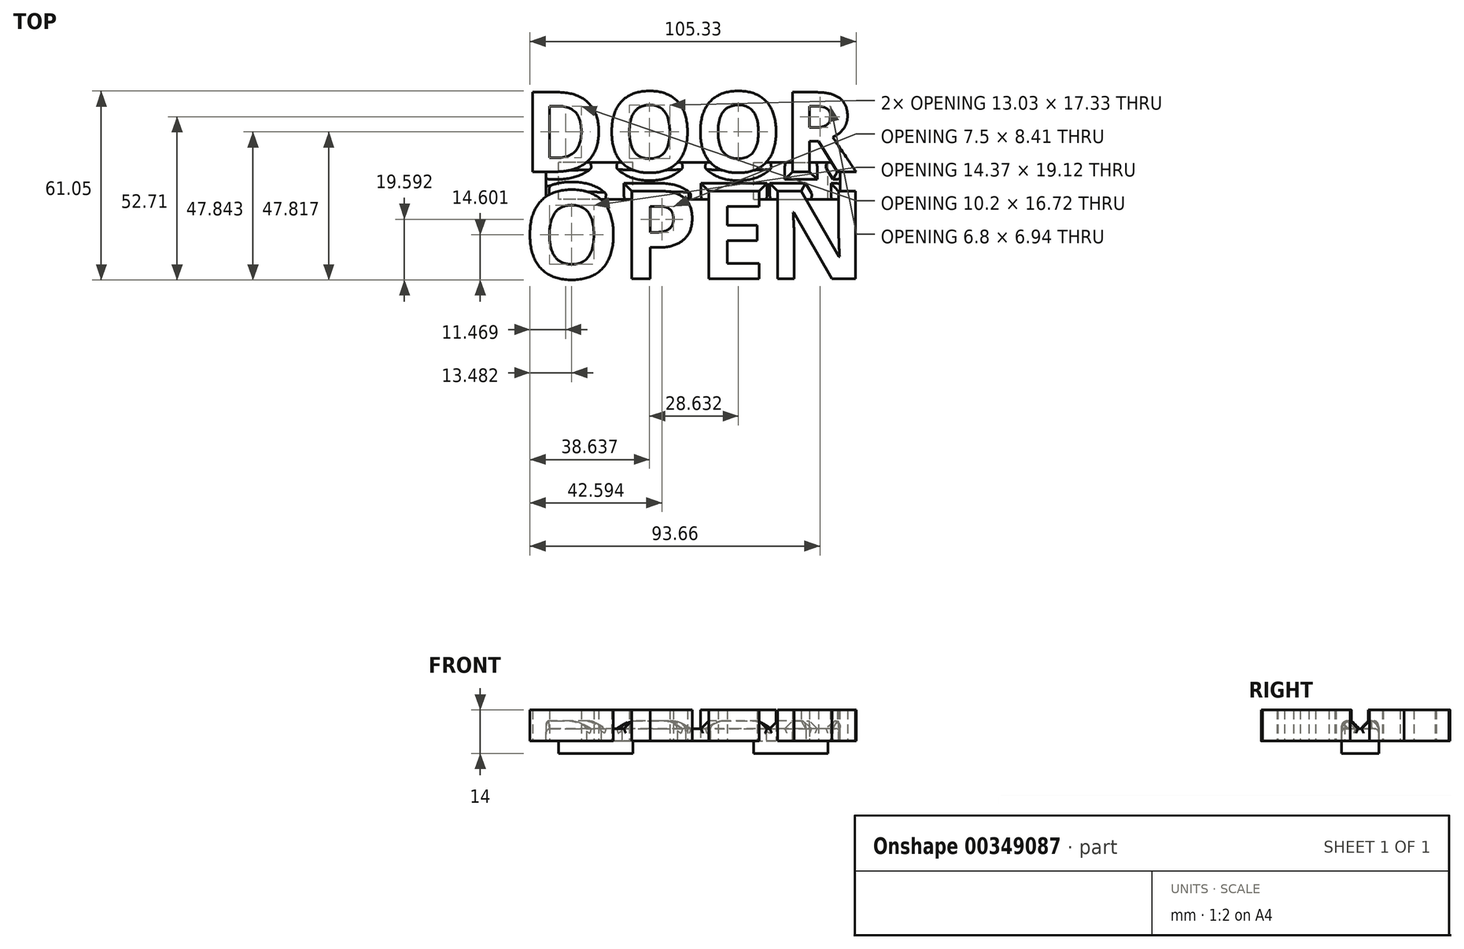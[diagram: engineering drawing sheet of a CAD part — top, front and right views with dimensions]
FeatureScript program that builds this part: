
annotation { "Feature Type Name" : "Feature", "Feature Type Description" : "" }
export const myFeature = defineFeature(function(context is Context, id is Id, definition is map)
    precondition{}
    {
        {
            var Q0;
            Q0=qCreatedBy(makeId("Top.planeOp"),FACE);
            var sketch = newSketch(context, id + "F0", { "sketchPlane" : qUnion([Q0])});
            skText(sketch, "E0", { "text": "DOOR", "fontName": "OpenSans-Bold.ttf"});
            skText(sketch, "E1", { "text": "OPEN", "fontName": "OpenSans-Bold.ttf"});
            skLineSegment(sketch, "E2", {"start": v(0, 3) * mm, "end": v(0, -3) * mm, "construction": true});
            skPoint(sketch, "E3", {"position": v(0, 0) * mm});
            const initialGuessF0  = {"E0": [-0.055, 0.003, 1, 0, 0.0259], "E1": [-0.055, -0.03157, 1, 0, 0.02857]};
            skSetInitialGuess(sketch, initialGuessF0);
            skSolve(sketch);
        }
        {
            var Q0;
            Q0=makeQuery(id+"F0.imprint","IMPRINT",FACE,{"disambiguationData":[TD([[makeQuery(id+"F0.imprint","IMPRINT",EDGE,{"derivedFrom":sQuery(id+"F0.wireOp",EDGE,"E0.sketch_text.stroke-0")}),-1.0]])]});
            var Q1;
            Q1=makeQuery(id+"F0.imprint","IMPRINT",FACE,{"disambiguationData":[TD([[makeQuery(id+"F0.imprint","IMPRINT",EDGE,{"derivedFrom":sQuery(id+"F0.wireOp",EDGE,"E0.sketch_text.stroke-12")}),-1.0]])]});
            var Q2;
            Q2=makeQuery(id+"F0.imprint","IMPRINT",FACE,{"disambiguationData":[TD([[makeQuery(id+"F0.imprint","IMPRINT",EDGE,{"derivedFrom":sQuery(id+"F0.wireOp",EDGE,"E0.sketch_text.stroke-26")}),-1.0]])]});
            var Q3;
            Q3=makeQuery(id+"F0.imprint","IMPRINT",FACE,{"disambiguationData":[TD([[makeQuery(id+"F0.imprint","IMPRINT",EDGE,{"derivedFrom":sQuery(id+"F0.wireOp",EDGE,"E0.sketch_text.stroke-40")}),-1.0]])]});
            var Q4;
            Q4=makeQuery(id+"F0.imprint","IMPRINT",FACE,{"disambiguationData":[TD([[makeQuery(id+"F0.imprint","IMPRINT",EDGE,{"derivedFrom":sQuery(id+"F0.wireOp",EDGE,"E1.sketch_text.stroke-0")}),-1.0]])]});
            var Q5;
            Q5=makeQuery(id+"F0.imprint","IMPRINT",FACE,{"disambiguationData":[TD([[makeQuery(id+"F0.imprint","IMPRINT",EDGE,{"derivedFrom":sQuery(id+"F0.wireOp",EDGE,"E1.sketch_text.stroke-14")}),-1.0]])]});
            var Q6;
            Q6=makeQuery(id+"F0.imprint","IMPRINT",FACE,{"disambiguationData":[TD([[makeQuery(id+"F0.imprint","IMPRINT",EDGE,{"derivedFrom":sQuery(id+"F0.wireOp",EDGE,"E1.sketch_text.stroke-30")}),-1.0]])]});
            var Q7;
            Q7=makeQuery(id+"F0.imprint","IMPRINT",FACE,{"disambiguationData":[TD([[makeQuery(id+"F0.imprint","IMPRINT",EDGE,{"derivedFrom":sQuery(id+"F0.wireOp",EDGE,"E1.sketch_text.stroke-42")}),-1.0]])]});
            extrude(context, id + "F1", {"entities" : qUnion([Q0, Q1, Q2, Q3, Q4, Q5, Q6, Q7]), "depth" : 10 * mm});
        }
        {
            var Q0;
            Q0=qCreatedBy(makeId("Top.planeOp"),FACE);
            var sketch = newSketch(context, id + "F2", { "sketchPlane" : qUnion([Q0])});
            skLineSegment(sketch, "E4.bottom", {"start": v(47.5, 6) * mm, "end": v(-47.5, 6) * mm});
            skLineSegment(sketch, "E4.top", {"start": v(47.5, -6) * mm, "end": v(-47.5, -6) * mm});
            skLineSegment(sketch, "E4.left", {"start": v(47.5, 6) * mm, "end": v(47.5, -6) * mm});
            skLineSegment(sketch, "E4.right", {"start": v(-47.5, 6) * mm, "end": v(-47.5, -6) * mm});
            skPoint(sketch, "E4.middle", {"position": v(0, 0) * mm});
            skSolve(sketch);
        }
        {
            var Q0;
            Q0=makeQuery(id+"F2.imprint","IMPRINT",FACE,{"disambiguationData":[TD([[makeQuery(id+"F2.imprint","IMPRINT",EDGE,{"derivedFrom":sQuery(id+"F2.wireOp",EDGE,"E4.bottom")}),1.0]])]});
            extrude(context, id + "F3", {"entities" : qUnion([Q0]), "operationType" : NewBodyOperationType.ADD, "depth" : 4 * mm});
        }
        {
            var Q0;
            Q0=makeQuery(id+"F3.boolean.opBoolean","INTERSECT",EDGE,{"derivedFrom":[makeQuery(id+"F1.opExtrude","SWEPT_FACE",FACE,{"disambiguationData":[OSD([sQuery(id+"F0.wireOp",EDGE,"E0.sketch_text.stroke-1")])]}),makeQuery(id+"F3.opExtrude","CAP_FACE",FACE,{"disambiguationData":[OSD([sQuery(id+"F2.wireOp",EDGE,"E4.bottom"),sQuery(id+"F2.wireOp",EDGE,"E4.top"),sQuery(id+"F2.wireOp",EDGE,"E4.left"),sQuery(id+"F2.wireOp",EDGE,"E4.right")])],"isStart":false})]});
            var Q1;
            Q1=makeQuery(id+"F3.boolean.opBoolean","INTERSECT",EDGE,{"derivedFrom":[makeQuery(id+"F1.opExtrude","SWEPT_FACE",FACE,{"disambiguationData":[OSD([sQuery(id+"F0.wireOp",EDGE,"E0.sketch_text.stroke-14")])]}),makeQuery(id+"F3.opExtrude","CAP_FACE",FACE,{"disambiguationData":[OSD([sQuery(id+"F2.wireOp",EDGE,"E4.bottom"),sQuery(id+"F2.wireOp",EDGE,"E4.top"),sQuery(id+"F2.wireOp",EDGE,"E4.left"),sQuery(id+"F2.wireOp",EDGE,"E4.right")])],"isStart":false})]});
            var Q2;
            Q2=makeQuery(id+"F3.boolean.opBoolean","INTERSECT",EDGE,{"derivedFrom":[makeQuery(id+"F1.opExtrude","SWEPT_FACE",FACE,{"disambiguationData":[OSD([sQuery(id+"F0.wireOp",EDGE,"E0.sketch_text.stroke-28")])]}),makeQuery(id+"F3.opExtrude","CAP_FACE",FACE,{"disambiguationData":[OSD([sQuery(id+"F2.wireOp",EDGE,"E4.bottom"),sQuery(id+"F2.wireOp",EDGE,"E4.top"),sQuery(id+"F2.wireOp",EDGE,"E4.left"),sQuery(id+"F2.wireOp",EDGE,"E4.right")])],"isStart":false})]});
            var Q3;
            Q3=makeQuery(id+"F3.boolean.opBoolean","INTERSECT",EDGE,{"derivedFrom":[makeQuery(id+"F1.opExtrude","SWEPT_FACE",FACE,{"disambiguationData":[OSD([sQuery(id+"F0.wireOp",EDGE,"E0.sketch_text.stroke-48")])]}),makeQuery(id+"F3.opExtrude","CAP_FACE",FACE,{"disambiguationData":[OSD([sQuery(id+"F2.wireOp",EDGE,"E4.bottom"),sQuery(id+"F2.wireOp",EDGE,"E4.top"),sQuery(id+"F2.wireOp",EDGE,"E4.left"),sQuery(id+"F2.wireOp",EDGE,"E4.right")])],"isStart":false})]});
            var Q4;
            Q4=makeQuery(id+"F3.boolean.opBoolean","INTERSECT",EDGE,{"derivedFrom":[makeQuery(id+"F1.opExtrude","SWEPT_FACE",FACE,{"disambiguationData":[OSD([sQuery(id+"F0.wireOp",EDGE,"E0.sketch_text.stroke-49")])]}),makeQuery(id+"F3.opExtrude","CAP_FACE",FACE,{"disambiguationData":[OSD([sQuery(id+"F2.wireOp",EDGE,"E4.bottom"),sQuery(id+"F2.wireOp",EDGE,"E4.top"),sQuery(id+"F2.wireOp",EDGE,"E4.left"),sQuery(id+"F2.wireOp",EDGE,"E4.right")])],"isStart":false})]});
            var Q5;
            Q5=makeQuery(id+"F3.boolean.opBoolean","INTERSECT",EDGE,{"derivedFrom":[makeQuery(id+"F1.opExtrude","SWEPT_FACE",FACE,{"disambiguationData":[OSD([sQuery(id+"F0.wireOp",EDGE,"E0.sketch_text.stroke-47")])]}),makeQuery(id+"F3.opExtrude","CAP_FACE",FACE,{"disambiguationData":[OSD([sQuery(id+"F2.wireOp",EDGE,"E4.bottom"),sQuery(id+"F2.wireOp",EDGE,"E4.top"),sQuery(id+"F2.wireOp",EDGE,"E4.left"),sQuery(id+"F2.wireOp",EDGE,"E4.right")])],"isStart":false})]});
            var Q6;
            Q6=makeQuery(id+"F3.boolean.opBoolean","INTERSECT",EDGE,{"derivedFrom":[makeQuery(id+"F1.opExtrude","SWEPT_FACE",FACE,{"disambiguationData":[OSD([sQuery(id+"F0.wireOp",EDGE,"E0.sketch_text.stroke-57")])]}),makeQuery(id+"F3.opExtrude","CAP_FACE",FACE,{"disambiguationData":[OSD([sQuery(id+"F2.wireOp",EDGE,"E4.bottom"),sQuery(id+"F2.wireOp",EDGE,"E4.top"),sQuery(id+"F2.wireOp",EDGE,"E4.left"),sQuery(id+"F2.wireOp",EDGE,"E4.right")])],"isStart":false})]});
            var Q7;
            Q7=makeQuery(id+"F3.boolean.opBoolean","INTERSECT",EDGE,{"derivedFrom":[makeQuery(id+"F1.opExtrude","SWEPT_FACE",FACE,{"disambiguationData":[OSD([sQuery(id+"F0.wireOp",EDGE,"E0.sketch_text.stroke-56")])]}),makeQuery(id+"F3.opExtrude","CAP_FACE",FACE,{"disambiguationData":[OSD([sQuery(id+"F2.wireOp",EDGE,"E4.bottom"),sQuery(id+"F2.wireOp",EDGE,"E4.top"),sQuery(id+"F2.wireOp",EDGE,"E4.left"),sQuery(id+"F2.wireOp",EDGE,"E4.right")])],"isStart":false})]});
            var Q8;
            Q8=makeQuery(id+"F3.boolean.opBoolean","INTERSECT",EDGE,{"derivedFrom":[makeQuery(id+"F1.opExtrude","SWEPT_FACE",FACE,{"disambiguationData":[OSD([sQuery(id+"F0.wireOp",EDGE,"E1.sketch_text.stroke-53")])]}),makeQuery(id+"F3.opExtrude","CAP_FACE",FACE,{"disambiguationData":[OSD([sQuery(id+"F2.wireOp",EDGE,"E4.bottom"),sQuery(id+"F2.wireOp",EDGE,"E4.top"),sQuery(id+"F2.wireOp",EDGE,"E4.left"),sQuery(id+"F2.wireOp",EDGE,"E4.right")])],"isStart":false})]});
            var Q9;
            Q9=makeQuery(id+"F3.boolean.opBoolean","INTERSECT",EDGE,{"derivedFrom":[makeQuery(id+"F1.opExtrude","SWEPT_FACE",FACE,{"disambiguationData":[OSD([sQuery(id+"F0.wireOp",EDGE,"E1.sketch_text.stroke-54")])]}),makeQuery(id+"F3.opExtrude","CAP_FACE",FACE,{"disambiguationData":[OSD([sQuery(id+"F2.wireOp",EDGE,"E4.bottom"),sQuery(id+"F2.wireOp",EDGE,"E4.top"),sQuery(id+"F2.wireOp",EDGE,"E4.left"),sQuery(id+"F2.wireOp",EDGE,"E4.right")])],"isStart":false})]});
            var Q10;
            Q10=makeQuery(id+"F3.boolean.opBoolean","INTERSECT",EDGE,{"derivedFrom":[makeQuery(id+"F1.opExtrude","SWEPT_FACE",FACE,{"disambiguationData":[OSD([sQuery(id+"F0.wireOp",EDGE,"E1.sketch_text.stroke-49")])]}),makeQuery(id+"F3.opExtrude","CAP_FACE",FACE,{"disambiguationData":[OSD([sQuery(id+"F2.wireOp",EDGE,"E4.bottom"),sQuery(id+"F2.wireOp",EDGE,"E4.top"),sQuery(id+"F2.wireOp",EDGE,"E4.left"),sQuery(id+"F2.wireOp",EDGE,"E4.right")])],"isStart":false})]});
            var Q11;
            Q11=makeQuery(id+"F3.boolean.opBoolean","INTERSECT",EDGE,{"derivedFrom":[makeQuery(id+"F1.opExtrude","SWEPT_FACE",FACE,{"disambiguationData":[OSD([sQuery(id+"F0.wireOp",EDGE,"E1.sketch_text.stroke-50")])]}),makeQuery(id+"F3.opExtrude","CAP_FACE",FACE,{"disambiguationData":[OSD([sQuery(id+"F2.wireOp",EDGE,"E4.bottom"),sQuery(id+"F2.wireOp",EDGE,"E4.top"),sQuery(id+"F2.wireOp",EDGE,"E4.left"),sQuery(id+"F2.wireOp",EDGE,"E4.right")])],"isStart":false})]});
            var Q12;
            Q12=makeQuery(id+"F3.boolean.opBoolean","INTERSECT",EDGE,{"derivedFrom":[makeQuery(id+"F1.opExtrude","SWEPT_FACE",FACE,{"disambiguationData":[OSD([sQuery(id+"F0.wireOp",EDGE,"E1.sketch_text.stroke-48")])]}),makeQuery(id+"F3.opExtrude","CAP_FACE",FACE,{"disambiguationData":[OSD([sQuery(id+"F2.wireOp",EDGE,"E4.bottom"),sQuery(id+"F2.wireOp",EDGE,"E4.top"),sQuery(id+"F2.wireOp",EDGE,"E4.left"),sQuery(id+"F2.wireOp",EDGE,"E4.right")])],"isStart":false})]});
            var Q13;
            Q13=makeQuery(id+"F3.boolean.opBoolean","INTERSECT",EDGE,{"derivedFrom":[makeQuery(id+"F1.opExtrude","SWEPT_FACE",FACE,{"disambiguationData":[OSD([sQuery(id+"F0.wireOp",EDGE,"E1.sketch_text.stroke-33")])]}),makeQuery(id+"F3.opExtrude","CAP_FACE",FACE,{"disambiguationData":[OSD([sQuery(id+"F2.wireOp",EDGE,"E4.bottom"),sQuery(id+"F2.wireOp",EDGE,"E4.top"),sQuery(id+"F2.wireOp",EDGE,"E4.left"),sQuery(id+"F2.wireOp",EDGE,"E4.right")])],"isStart":false})]});
            var Q14;
            Q14=makeQuery(id+"F3.boolean.opBoolean","INTERSECT",EDGE,{"derivedFrom":[makeQuery(id+"F1.opExtrude","SWEPT_FACE",FACE,{"disambiguationData":[OSD([sQuery(id+"F0.wireOp",EDGE,"E1.sketch_text.stroke-32")])]}),makeQuery(id+"F3.opExtrude","CAP_FACE",FACE,{"disambiguationData":[OSD([sQuery(id+"F2.wireOp",EDGE,"E4.bottom"),sQuery(id+"F2.wireOp",EDGE,"E4.top"),sQuery(id+"F2.wireOp",EDGE,"E4.left"),sQuery(id+"F2.wireOp",EDGE,"E4.right")])],"isStart":false})]});
            var Q15;
            Q15=makeQuery(id+"F3.boolean.opBoolean","INTERSECT",EDGE,{"derivedFrom":[makeQuery(id+"F1.opExtrude","SWEPT_FACE",FACE,{"disambiguationData":[OSD([sQuery(id+"F0.wireOp",EDGE,"E1.sketch_text.stroke-31")])]}),makeQuery(id+"F3.opExtrude","CAP_FACE",FACE,{"disambiguationData":[OSD([sQuery(id+"F2.wireOp",EDGE,"E4.bottom"),sQuery(id+"F2.wireOp",EDGE,"E4.top"),sQuery(id+"F2.wireOp",EDGE,"E4.left"),sQuery(id+"F2.wireOp",EDGE,"E4.right")])],"isStart":false})]});
            var Q16;
            Q16=makeQuery(id+"F3.boolean.opBoolean","INTERSECT",EDGE,{"derivedFrom":[makeQuery(id+"F1.opExtrude","SWEPT_FACE",FACE,{"disambiguationData":[OSD([sQuery(id+"F0.wireOp",EDGE,"E1.sketch_text.stroke-27")])]}),makeQuery(id+"F3.opExtrude","CAP_FACE",FACE,{"disambiguationData":[OSD([sQuery(id+"F2.wireOp",EDGE,"E4.bottom"),sQuery(id+"F2.wireOp",EDGE,"E4.top"),sQuery(id+"F2.wireOp",EDGE,"E4.left"),sQuery(id+"F2.wireOp",EDGE,"E4.right")])],"isStart":false})]});
            var Q17;
            Q17=makeQuery(id+"F3.boolean.opBoolean","INTERSECT",EDGE,{"derivedFrom":[makeQuery(id+"F1.opExtrude","SWEPT_FACE",FACE,{"disambiguationData":[OSD([sQuery(id+"F0.wireOp",EDGE,"E1.sketch_text.stroke-26")])]}),makeQuery(id+"F3.opExtrude","CAP_FACE",FACE,{"disambiguationData":[OSD([sQuery(id+"F2.wireOp",EDGE,"E4.bottom"),sQuery(id+"F2.wireOp",EDGE,"E4.top"),sQuery(id+"F2.wireOp",EDGE,"E4.left"),sQuery(id+"F2.wireOp",EDGE,"E4.right")])],"isStart":false})]});
            var Q18;
            Q18=makeQuery(id+"F3.boolean.opBoolean","INTERSECT",EDGE,{"derivedFrom":[makeQuery(id+"F1.opExtrude","SWEPT_FACE",FACE,{"disambiguationData":[OSD([sQuery(id+"F0.wireOp",EDGE,"E1.sketch_text.stroke-6")])]}),makeQuery(id+"F3.opExtrude","CAP_FACE",FACE,{"disambiguationData":[OSD([sQuery(id+"F2.wireOp",EDGE,"E4.bottom"),sQuery(id+"F2.wireOp",EDGE,"E4.top"),sQuery(id+"F2.wireOp",EDGE,"E4.left"),sQuery(id+"F2.wireOp",EDGE,"E4.right")])],"isStart":false})]});
            chamfer(context, id + "F4", {"entities" : qUnion([Q0, Q1, Q2, Q3, Q4, Q5, Q6, Q7, Q8, Q9, Q10, Q11, Q12, Q13, Q14, Q15, Q16, Q17, Q18]), "width" : 2.5 * mm, "tangentPropagation" : true});
        }
        {
            var Q0;
            Q0=makeQuery(id+"F3.boolean.opBoolean","MERGE",FACE,{"derivedFrom":[makeQuery(id+"F1.opExtrude","CAP_FACE",FACE,{"disambiguationData":[OSD([sQuery(id+"F0.wireOp",EDGE,"E0.sketch_text.stroke-0"),sQuery(id+"F0.wireOp",EDGE,"E0.sketch_text.stroke-1"),sQuery(id+"F0.wireOp",EDGE,"E0.sketch_text.stroke-2"),sQuery(id+"F0.wireOp",EDGE,"E0.sketch_text.stroke-3"),sQuery(id+"F0.wireOp",EDGE,"E0.sketch_text.stroke-4"),sQuery(id+"F0.wireOp",EDGE,"E0.sketch_text.stroke-5"),sQuery(id+"F0.wireOp",EDGE,"E0.sketch_text.stroke-6"),sQuery(id+"F0.wireOp",EDGE,"E0.sketch_text.stroke-7"),sQuery(id+"F0.wireOp",EDGE,"E0.sketch_text.stroke-8"),sQuery(id+"F0.wireOp",EDGE,"E0.sketch_text.stroke-9"),sQuery(id+"F0.wireOp",EDGE,"E0.sketch_text.stroke-10"),sQuery(id+"F0.wireOp",EDGE,"E0.sketch_text.stroke-11")])],"isStart":true}),makeQuery(id+"F1.opExtrude","CAP_FACE",FACE,{"disambiguationData":[OSD([sQuery(id+"F0.wireOp",EDGE,"E0.sketch_text.stroke-12"),sQuery(id+"F0.wireOp",EDGE,"E0.sketch_text.stroke-13"),sQuery(id+"F0.wireOp",EDGE,"E0.sketch_text.stroke-14"),sQuery(id+"F0.wireOp",EDGE,"E0.sketch_text.stroke-15"),sQuery(id+"F0.wireOp",EDGE,"E0.sketch_text.stroke-16"),sQuery(id+"F0.wireOp",EDGE,"E0.sketch_text.stroke-17"),sQuery(id+"F0.wireOp",EDGE,"E0.sketch_text.stroke-18"),sQuery(id+"F0.wireOp",EDGE,"E0.sketch_text.stroke-19"),sQuery(id+"F0.wireOp",EDGE,"E0.sketch_text.stroke-20"),sQuery(id+"F0.wireOp",EDGE,"E0.sketch_text.stroke-21"),sQuery(id+"F0.wireOp",EDGE,"E0.sketch_text.stroke-22"),sQuery(id+"F0.wireOp",EDGE,"E0.sketch_text.stroke-23"),sQuery(id+"F0.wireOp",EDGE,"E0.sketch_text.stroke-24"),sQuery(id+"F0.wireOp",EDGE,"E0.sketch_text.stroke-25")])],"isStart":true}),makeQuery(id+"F1.opExtrude","CAP_FACE",FACE,{"disambiguationData":[OSD([sQuery(id+"F0.wireOp",EDGE,"E0.sketch_text.stroke-26"),sQuery(id+"F0.wireOp",EDGE,"E0.sketch_text.stroke-27"),sQuery(id+"F0.wireOp",EDGE,"E0.sketch_text.stroke-28"),sQuery(id+"F0.wireOp",EDGE,"E0.sketch_text.stroke-29"),sQuery(id+"F0.wireOp",EDGE,"E0.sketch_text.stroke-30"),sQuery(id+"F0.wireOp",EDGE,"E0.sketch_text.stroke-31"),sQuery(id+"F0.wireOp",EDGE,"E0.sketch_text.stroke-32"),sQuery(id+"F0.wireOp",EDGE,"E0.sketch_text.stroke-33"),sQuery(id+"F0.wireOp",EDGE,"E0.sketch_text.stroke-34"),sQuery(id+"F0.wireOp",EDGE,"E0.sketch_text.stroke-35"),sQuery(id+"F0.wireOp",EDGE,"E0.sketch_text.stroke-36"),sQuery(id+"F0.wireOp",EDGE,"E0.sketch_text.stroke-37"),sQuery(id+"F0.wireOp",EDGE,"E0.sketch_text.stroke-38"),sQuery(id+"F0.wireOp",EDGE,"E0.sketch_text.stroke-39")])],"isStart":true}),makeQuery(id+"F1.opExtrude","CAP_FACE",FACE,{"disambiguationData":[OSD([sQuery(id+"F0.wireOp",EDGE,"E0.sketch_text.stroke-40"),sQuery(id+"F0.wireOp",EDGE,"E0.sketch_text.stroke-41"),sQuery(id+"F0.wireOp",EDGE,"E0.sketch_text.stroke-42"),sQuery(id+"F0.wireOp",EDGE,"E0.sketch_text.stroke-43"),sQuery(id+"F0.wireOp",EDGE,"E0.sketch_text.stroke-44"),sQuery(id+"F0.wireOp",EDGE,"E0.sketch_text.stroke-45"),sQuery(id+"F0.wireOp",EDGE,"E0.sketch_text.stroke-46"),sQuery(id+"F0.wireOp",EDGE,"E0.sketch_text.stroke-47"),sQuery(id+"F0.wireOp",EDGE,"E0.sketch_text.stroke-48"),sQuery(id+"F0.wireOp",EDGE,"E0.sketch_text.stroke-49"),sQuery(id+"F0.wireOp",EDGE,"E0.sketch_text.stroke-50"),sQuery(id+"F0.wireOp",EDGE,"E0.sketch_text.stroke-51"),sQuery(id+"F0.wireOp",EDGE,"E0.sketch_text.stroke-52"),sQuery(id+"F0.wireOp",EDGE,"E0.sketch_text.stroke-53"),sQuery(id+"F0.wireOp",EDGE,"E0.sketch_text.stroke-54"),sQuery(id+"F0.wireOp",EDGE,"E0.sketch_text.stroke-55"),sQuery(id+"F0.wireOp",EDGE,"E0.sketch_text.stroke-56"),sQuery(id+"F0.wireOp",EDGE,"E0.sketch_text.stroke-57"),sQuery(id+"F0.wireOp",EDGE,"E0.sketch_text.stroke-58")])],"isStart":true}),makeQuery(id+"F1.opExtrude","CAP_FACE",FACE,{"disambiguationData":[OSD([sQuery(id+"F0.wireOp",EDGE,"E1.sketch_text.stroke-0"),sQuery(id+"F0.wireOp",EDGE,"E1.sketch_text.stroke-1"),sQuery(id+"F0.wireOp",EDGE,"E1.sketch_text.stroke-2"),sQuery(id+"F0.wireOp",EDGE,"E1.sketch_text.stroke-3"),sQuery(id+"F0.wireOp",EDGE,"E1.sketch_text.stroke-4"),sQuery(id+"F0.wireOp",EDGE,"E1.sketch_text.stroke-5"),sQuery(id+"F0.wireOp",EDGE,"E1.sketch_text.stroke-6"),sQuery(id+"F0.wireOp",EDGE,"E1.sketch_text.stroke-7"),sQuery(id+"F0.wireOp",EDGE,"E1.sketch_text.stroke-8"),sQuery(id+"F0.wireOp",EDGE,"E1.sketch_text.stroke-9"),sQuery(id+"F0.wireOp",EDGE,"E1.sketch_text.stroke-10"),sQuery(id+"F0.wireOp",EDGE,"E1.sketch_text.stroke-11"),sQuery(id+"F0.wireOp",EDGE,"E1.sketch_text.stroke-12"),sQuery(id+"F0.wireOp",EDGE,"E1.sketch_text.stroke-13")])],"isStart":true}),makeQuery(id+"F1.opExtrude","CAP_FACE",FACE,{"disambiguationData":[OSD([sQuery(id+"F0.wireOp",EDGE,"E1.sketch_text.stroke-14"),sQuery(id+"F0.wireOp",EDGE,"E1.sketch_text.stroke-15"),sQuery(id+"F0.wireOp",EDGE,"E1.sketch_text.stroke-16"),sQuery(id+"F0.wireOp",EDGE,"E1.sketch_text.stroke-17"),sQuery(id+"F0.wireOp",EDGE,"E1.sketch_text.stroke-18"),sQuery(id+"F0.wireOp",EDGE,"E1.sketch_text.stroke-19"),sQuery(id+"F0.wireOp",EDGE,"E1.sketch_text.stroke-20"),sQuery(id+"F0.wireOp",EDGE,"E1.sketch_text.stroke-21"),sQuery(id+"F0.wireOp",EDGE,"E1.sketch_text.stroke-22"),sQuery(id+"F0.wireOp",EDGE,"E1.sketch_text.stroke-23"),sQuery(id+"F0.wireOp",EDGE,"E1.sketch_text.stroke-24"),sQuery(id+"F0.wireOp",EDGE,"E1.sketch_text.stroke-25"),sQuery(id+"F0.wireOp",EDGE,"E1.sketch_text.stroke-26"),sQuery(id+"F0.wireOp",EDGE,"E1.sketch_text.stroke-27"),sQuery(id+"F0.wireOp",EDGE,"E1.sketch_text.stroke-28"),sQuery(id+"F0.wireOp",EDGE,"E1.sketch_text.stroke-29")])],"isStart":true}),makeQuery(id+"F1.opExtrude","CAP_FACE",FACE,{"disambiguationData":[OSD([sQuery(id+"F0.wireOp",EDGE,"E1.sketch_text.stroke-30"),sQuery(id+"F0.wireOp",EDGE,"E1.sketch_text.stroke-31"),sQuery(id+"F0.wireOp",EDGE,"E1.sketch_text.stroke-32"),sQuery(id+"F0.wireOp",EDGE,"E1.sketch_text.stroke-33"),sQuery(id+"F0.wireOp",EDGE,"E1.sketch_text.stroke-34"),sQuery(id+"F0.wireOp",EDGE,"E1.sketch_text.stroke-35"),sQuery(id+"F0.wireOp",EDGE,"E1.sketch_text.stroke-36"),sQuery(id+"F0.wireOp",EDGE,"E1.sketch_text.stroke-37"),sQuery(id+"F0.wireOp",EDGE,"E1.sketch_text.stroke-38"),sQuery(id+"F0.wireOp",EDGE,"E1.sketch_text.stroke-39"),sQuery(id+"F0.wireOp",EDGE,"E1.sketch_text.stroke-40"),sQuery(id+"F0.wireOp",EDGE,"E1.sketch_text.stroke-41")])],"isStart":true}),makeQuery(id+"F1.opExtrude","CAP_FACE",FACE,{"disambiguationData":[OSD([sQuery(id+"F0.wireOp",EDGE,"E1.sketch_text.stroke-42"),sQuery(id+"F0.wireOp",EDGE,"E1.sketch_text.stroke-43"),sQuery(id+"F0.wireOp",EDGE,"E1.sketch_text.stroke-44"),sQuery(id+"F0.wireOp",EDGE,"E1.sketch_text.stroke-45"),sQuery(id+"F0.wireOp",EDGE,"E1.sketch_text.stroke-46"),sQuery(id+"F0.wireOp",EDGE,"E1.sketch_text.stroke-47"),sQuery(id+"F0.wireOp",EDGE,"E1.sketch_text.stroke-48"),sQuery(id+"F0.wireOp",EDGE,"E1.sketch_text.stroke-49"),sQuery(id+"F0.wireOp",EDGE,"E1.sketch_text.stroke-50"),sQuery(id+"F0.wireOp",EDGE,"E1.sketch_text.stroke-51"),sQuery(id+"F0.wireOp",EDGE,"E1.sketch_text.stroke-52"),sQuery(id+"F0.wireOp",EDGE,"E1.sketch_text.stroke-53"),sQuery(id+"F0.wireOp",EDGE,"E1.sketch_text.stroke-54"),sQuery(id+"F0.wireOp",EDGE,"E1.sketch_text.stroke-55")])],"isStart":true}),makeQuery(id+"F3.opExtrude","CAP_FACE",FACE,{"disambiguationData":[OSD([sQuery(id+"F2.wireOp",EDGE,"E4.bottom"),sQuery(id+"F2.wireOp",EDGE,"E4.top"),sQuery(id+"F2.wireOp",EDGE,"E4.left"),sQuery(id+"F2.wireOp",EDGE,"E4.right")])],"isStart":true})]});
            var sketch = newSketch(context, id + "F5", { "sketchPlane" : qUnion([Q0])});
            skLineSegment(sketch, "E5.bottom", {"start": v(19.5, 6) * mm, "end": v(43.5, 6) * mm});
            skLineSegment(sketch, "E5.top", {"start": v(19.5, -6) * mm, "end": v(43.5, -6) * mm});
            skLineSegment(sketch, "E5.left", {"start": v(19.5, 6) * mm, "end": v(19.5, -6) * mm});
            skLineSegment(sketch, "E5.right", {"start": v(43.5, 6) * mm, "end": v(43.5, -6) * mm});
            skPoint(sketch, "E5.middle", {"position": v(31.5, 0) * mm});
            skLineSegment(sketch, "E6.MirrorCS", {"start": v(-19.5, 6) * mm, "end": v(-43.5, 6) * mm});
            skLineSegment(sketch, "E7.MirrorCS", {"start": v(-43.5, 6) * mm, "end": v(-43.5, -6) * mm});
            skLineSegment(sketch, "E8.MirrorCS", {"start": v(-19.5, -6) * mm, "end": v(-43.5, -6) * mm});
            skLineSegment(sketch, "E9.MirrorCS", {"start": v(-19.5, 6) * mm, "end": v(-19.5, -6) * mm});
            skSolve(sketch);
        }
        {
            var Q0;
            {var subQ7=sQuery(id+"F5.wireOp",EDGE,"E5.left");Q0=makeQuery(id+"F5.imprint","IMPRINT",FACE,{"disambiguationData":[TD([[makeQuery(id+"F5.imprint","IMPRINT",EDGE,{"derivedFrom":subQ7}),1.0]])]});}
            var Q1;
            {var subQ0=sQuery(id+"F5.wireOp",EDGE,"E7.MirrorCS");Q1=makeQuery(id+"F5.imprint","IMPRINT",FACE,{"disambiguationData":[TD([[makeQuery(id+"F5.imprint","IMPRINT",EDGE,{"derivedFrom":subQ0}),1.0]])]});}
            extrude(context, id + "F6", {"entities" : qUnion([Q0, Q1]), "operationType" : NewBodyOperationType.ADD, "depth" : 4 * mm});
        }
        {
            var Q0;
            {var subQ0=sQuery(id+"F0.wireOp",EDGE,"E0.sketch_text.stroke-1");var subQ1=makeQuery(id+"F1.opExtrude","SWEPT_FACE",FACE,{"disambiguationData":[OSD([subQ0])]});var subQ3=sQuery(id+"F2.wireOp",EDGE,"E4.right");var subQ4=sQuery(id+"F2.wireOp",EDGE,"E4.left");var subQ5=sQuery(id+"F2.wireOp",EDGE,"E4.top");var subQ6=sQuery(id+"F2.wireOp",EDGE,"E4.bottom");var subQ7=makeQuery(id+"F3.opExtrude","CAP_FACE",FACE,{"disambiguationData":[OSD([subQ6,subQ5,subQ4,subQ3])],"isStart":false});Q0=makeQuery(id+"F4.opChamfer","BLEND_EDGE",EDGE,{"blendedFrom":[makeQuery(id+"F3.boolean.opBoolean","INTERSECT",EDGE,{"derivedFrom":[subQ1,subQ7]}),makeQuery(id+"F3.boolean.opBoolean","SPLIT",FACE,{"disambiguationData":[TD([subQ1])],"derivedFrom":makeQuery(id+"F3.opExtrude","SWEPT_FACE",FACE,{"disambiguationData":[OSD([subQ6])]})})],"blendedInto":[makeQuery(id+"F3.boolean.opBoolean","SPLIT",FACE,{"disambiguationData":[TD([subQ1])],"derivedFrom":makeQuery(id+"F3.opExtrude","SWEPT_FACE",FACE,{"disambiguationData":[OSD([subQ6])]})})]});}
            var Q1;
            {var subQ0=sQuery(id+"F2.wireOp",EDGE,"E4.bottom");Q1=makeQuery(id+"F3.boolean.opBoolean","SPLIT",EDGE,{"disambiguationData":[TD([makeQuery(id+"F1.opExtrude","SWEPT_FACE",FACE,{"disambiguationData":[OSD([sQuery(id+"F0.wireOp",EDGE,"E0.sketch_text.stroke-1")])]})])],"derivedFrom":makeQuery(id+"F3.opExtrude","CAP_EDGE",EDGE,{"disambiguationData":[OSD([subQ0])],"isStart":false})});}
            var Q2;
            {var subQ0=sQuery(id+"F0.wireOp",EDGE,"E0.sketch_text.stroke-1");var subQ1=sQuery(id+"F0.wireOp",EDGE,"E0.sketch_text.stroke-14");var subQ2=makeQuery(id+"F1.opExtrude","SWEPT_FACE",FACE,{"disambiguationData":[OSD([subQ1])]});var subQ3=sQuery(id+"F2.wireOp",EDGE,"E4.right");var subQ4=sQuery(id+"F2.wireOp",EDGE,"E4.left");var subQ5=sQuery(id+"F2.wireOp",EDGE,"E4.top");var subQ6=sQuery(id+"F2.wireOp",EDGE,"E4.bottom");var subQ7=makeQuery(id+"F3.opExtrude","CAP_FACE",FACE,{"disambiguationData":[OSD([subQ6,subQ5,subQ4,subQ3])],"isStart":false});Q2=makeQuery(id+"F4.opChamfer","BLEND_EDGE",EDGE,{"blendedFrom":[makeQuery(id+"F3.boolean.opBoolean","INTERSECT",EDGE,{"derivedFrom":[subQ2,subQ7]}),makeQuery(id+"F3.boolean.opBoolean","SPLIT",FACE,{"disambiguationData":[TD([makeQuery(id+"F1.opExtrude","SWEPT_FACE",FACE,{"disambiguationData":[OSD([subQ0])]})])],"derivedFrom":makeQuery(id+"F3.opExtrude","SWEPT_FACE",FACE,{"disambiguationData":[OSD([subQ6])]})})],"blendedInto":[makeQuery(id+"F3.boolean.opBoolean","SPLIT",FACE,{"disambiguationData":[TD([makeQuery(id+"F1.opExtrude","SWEPT_FACE",FACE,{"disambiguationData":[OSD([subQ0])]})])],"derivedFrom":makeQuery(id+"F3.opExtrude","SWEPT_FACE",FACE,{"disambiguationData":[OSD([subQ6])]})})]});}
            var Q3;
            {var subQ0=sQuery(id+"F0.wireOp",EDGE,"E0.sketch_text.stroke-13");var subQ2=makeQuery(id+"F1.opExtrude","SWEPT_FACE",FACE,{"disambiguationData":[OSD([subQ0])]});var subQ3=sQuery(id+"F2.wireOp",EDGE,"E4.right");var subQ4=sQuery(id+"F2.wireOp",EDGE,"E4.left");var subQ5=sQuery(id+"F2.wireOp",EDGE,"E4.top");var subQ6=sQuery(id+"F2.wireOp",EDGE,"E4.bottom");var subQ7=makeQuery(id+"F3.opExtrude","CAP_FACE",FACE,{"disambiguationData":[OSD([subQ6,subQ5,subQ4,subQ3])],"isStart":false});Q3=makeQuery(id+"F4.opChamfer","BLEND_EDGE",EDGE,{"blendedFrom":[makeQuery(id+"F3.boolean.opBoolean","INTERSECT",EDGE,{"derivedFrom":[subQ2,subQ7]}),makeQuery(id+"F3.boolean.opBoolean","SPLIT",FACE,{"disambiguationData":[TD([subQ2])],"derivedFrom":makeQuery(id+"F3.opExtrude","SWEPT_FACE",FACE,{"disambiguationData":[OSD([subQ6])]})})],"blendedInto":[makeQuery(id+"F3.boolean.opBoolean","SPLIT",FACE,{"disambiguationData":[TD([subQ2])],"derivedFrom":makeQuery(id+"F3.opExtrude","SWEPT_FACE",FACE,{"disambiguationData":[OSD([subQ6])]})})]});}
            var Q4;
            {var subQ0=sQuery(id+"F2.wireOp",EDGE,"E4.bottom");Q4=makeQuery(id+"F3.boolean.opBoolean","SPLIT",EDGE,{"disambiguationData":[TD([makeQuery(id+"F1.opExtrude","SWEPT_FACE",FACE,{"disambiguationData":[OSD([sQuery(id+"F0.wireOp",EDGE,"E0.sketch_text.stroke-13")])]})])],"derivedFrom":makeQuery(id+"F3.opExtrude","CAP_EDGE",EDGE,{"disambiguationData":[OSD([subQ0])],"isStart":false})});}
            var Q5;
            {var subQ0=sQuery(id+"F0.wireOp",EDGE,"E0.sketch_text.stroke-13");var subQ1=sQuery(id+"F0.wireOp",EDGE,"E0.sketch_text.stroke-28");var subQ2=makeQuery(id+"F1.opExtrude","SWEPT_FACE",FACE,{"disambiguationData":[OSD([subQ1])]});var subQ3=sQuery(id+"F2.wireOp",EDGE,"E4.right");var subQ4=sQuery(id+"F2.wireOp",EDGE,"E4.left");var subQ5=sQuery(id+"F2.wireOp",EDGE,"E4.top");var subQ6=sQuery(id+"F2.wireOp",EDGE,"E4.bottom");var subQ7=makeQuery(id+"F3.opExtrude","CAP_FACE",FACE,{"disambiguationData":[OSD([subQ6,subQ5,subQ4,subQ3])],"isStart":false});Q5=makeQuery(id+"F4.opChamfer","BLEND_EDGE",EDGE,{"blendedFrom":[makeQuery(id+"F3.boolean.opBoolean","INTERSECT",EDGE,{"derivedFrom":[subQ2,subQ7]}),makeQuery(id+"F3.boolean.opBoolean","SPLIT",FACE,{"disambiguationData":[TD([makeQuery(id+"F1.opExtrude","SWEPT_FACE",FACE,{"disambiguationData":[OSD([subQ0])]})])],"derivedFrom":makeQuery(id+"F3.opExtrude","SWEPT_FACE",FACE,{"disambiguationData":[OSD([subQ6])]})})],"blendedInto":[makeQuery(id+"F3.boolean.opBoolean","SPLIT",FACE,{"disambiguationData":[TD([makeQuery(id+"F1.opExtrude","SWEPT_FACE",FACE,{"disambiguationData":[OSD([subQ0])]})])],"derivedFrom":makeQuery(id+"F3.opExtrude","SWEPT_FACE",FACE,{"disambiguationData":[OSD([subQ6])]})})]});}
            var Q6;
            {var subQ1=sQuery(id+"F0.wireOp",EDGE,"E0.sketch_text.stroke-27");var subQ2=makeQuery(id+"F1.opExtrude","SWEPT_FACE",FACE,{"disambiguationData":[OSD([subQ1])]});var subQ3=sQuery(id+"F2.wireOp",EDGE,"E4.right");var subQ4=sQuery(id+"F2.wireOp",EDGE,"E4.left");var subQ5=sQuery(id+"F2.wireOp",EDGE,"E4.top");var subQ6=sQuery(id+"F2.wireOp",EDGE,"E4.bottom");var subQ7=makeQuery(id+"F3.opExtrude","CAP_FACE",FACE,{"disambiguationData":[OSD([subQ6,subQ5,subQ4,subQ3])],"isStart":false});Q6=makeQuery(id+"F4.opChamfer","BLEND_EDGE",EDGE,{"blendedFrom":[makeQuery(id+"F3.boolean.opBoolean","INTERSECT",EDGE,{"derivedFrom":[subQ2,subQ7]}),makeQuery(id+"F3.boolean.opBoolean","SPLIT",FACE,{"disambiguationData":[TD([subQ2])],"derivedFrom":makeQuery(id+"F3.opExtrude","SWEPT_FACE",FACE,{"disambiguationData":[OSD([subQ6])]})})],"blendedInto":[makeQuery(id+"F3.boolean.opBoolean","SPLIT",FACE,{"disambiguationData":[TD([subQ2])],"derivedFrom":makeQuery(id+"F3.opExtrude","SWEPT_FACE",FACE,{"disambiguationData":[OSD([subQ6])]})})]});}
            var Q7;
            {var subQ0=sQuery(id+"F2.wireOp",EDGE,"E4.bottom");Q7=makeQuery(id+"F3.boolean.opBoolean","SPLIT",EDGE,{"disambiguationData":[TD([makeQuery(id+"F1.opExtrude","SWEPT_FACE",FACE,{"disambiguationData":[OSD([sQuery(id+"F0.wireOp",EDGE,"E0.sketch_text.stroke-27")])]})])],"derivedFrom":makeQuery(id+"F3.opExtrude","CAP_EDGE",EDGE,{"disambiguationData":[OSD([subQ0])],"isStart":false})});}
            var Q8;
            {var subQ0=sQuery(id+"F0.wireOp",EDGE,"E0.sketch_text.stroke-49");var subQ1=makeQuery(id+"F1.opExtrude","SWEPT_FACE",FACE,{"disambiguationData":[OSD([subQ0])]});var subQ2=sQuery(id+"F0.wireOp",EDGE,"E0.sketch_text.stroke-27");var subQ3=sQuery(id+"F2.wireOp",EDGE,"E4.right");var subQ4=sQuery(id+"F2.wireOp",EDGE,"E4.left");var subQ5=sQuery(id+"F2.wireOp",EDGE,"E4.top");var subQ6=sQuery(id+"F2.wireOp",EDGE,"E4.bottom");var subQ7=makeQuery(id+"F3.opExtrude","CAP_FACE",FACE,{"disambiguationData":[OSD([subQ6,subQ5,subQ4,subQ3])],"isStart":false});Q8=makeQuery(id+"F4.opChamfer","BLEND_EDGE",EDGE,{"blendedFrom":[makeQuery(id+"F3.boolean.opBoolean","INTERSECT",EDGE,{"derivedFrom":[subQ1,subQ7]}),makeQuery(id+"F3.boolean.opBoolean","SPLIT",FACE,{"disambiguationData":[TD([makeQuery(id+"F1.opExtrude","SWEPT_FACE",FACE,{"disambiguationData":[OSD([subQ2])]})])],"derivedFrom":makeQuery(id+"F3.opExtrude","SWEPT_FACE",FACE,{"disambiguationData":[OSD([subQ6])]})})],"blendedInto":[makeQuery(id+"F3.boolean.opBoolean","SPLIT",FACE,{"disambiguationData":[TD([makeQuery(id+"F1.opExtrude","SWEPT_FACE",FACE,{"disambiguationData":[OSD([subQ2])]})])],"derivedFrom":makeQuery(id+"F3.opExtrude","SWEPT_FACE",FACE,{"disambiguationData":[OSD([subQ6])]})})]});}
            var Q9;
            {var subQ1=sQuery(id+"F0.wireOp",EDGE,"E0.sketch_text.stroke-47");var subQ2=makeQuery(id+"F1.opExtrude","SWEPT_FACE",FACE,{"disambiguationData":[OSD([subQ1])]});var subQ3=sQuery(id+"F2.wireOp",EDGE,"E4.right");var subQ4=sQuery(id+"F2.wireOp",EDGE,"E4.left");var subQ5=sQuery(id+"F2.wireOp",EDGE,"E4.top");var subQ6=sQuery(id+"F2.wireOp",EDGE,"E4.bottom");var subQ7=makeQuery(id+"F3.opExtrude","CAP_FACE",FACE,{"disambiguationData":[OSD([subQ6,subQ5,subQ4,subQ3])],"isStart":false});Q9=makeQuery(id+"F4.opChamfer","BLEND_EDGE",EDGE,{"blendedFrom":[makeQuery(id+"F3.boolean.opBoolean","INTERSECT",EDGE,{"derivedFrom":[subQ2,subQ7]}),makeQuery(id+"F3.boolean.opBoolean","SPLIT",FACE,{"disambiguationData":[TD([subQ2])],"derivedFrom":makeQuery(id+"F3.opExtrude","SWEPT_FACE",FACE,{"disambiguationData":[OSD([subQ6])]})})],"blendedInto":[makeQuery(id+"F3.boolean.opBoolean","SPLIT",FACE,{"disambiguationData":[TD([subQ2])],"derivedFrom":makeQuery(id+"F3.opExtrude","SWEPT_FACE",FACE,{"disambiguationData":[OSD([subQ6])]})})]});}
            var Q10;
            {var subQ0=sQuery(id+"F2.wireOp",EDGE,"E4.bottom");Q10=makeQuery(id+"F3.boolean.opBoolean","SPLIT",EDGE,{"disambiguationData":[TD([makeQuery(id+"F1.opExtrude","SWEPT_FACE",FACE,{"disambiguationData":[OSD([sQuery(id+"F0.wireOp",EDGE,"E0.sketch_text.stroke-47")])]})])],"derivedFrom":makeQuery(id+"F3.opExtrude","CAP_EDGE",EDGE,{"disambiguationData":[OSD([subQ0])],"isStart":false})});}
            var Q11;
            {var subQ0=sQuery(id+"F0.wireOp",EDGE,"E0.sketch_text.stroke-57");var subQ1=sQuery(id+"F0.wireOp",EDGE,"E0.sketch_text.stroke-47");var subQ2=makeQuery(id+"F1.opExtrude","SWEPT_FACE",FACE,{"disambiguationData":[OSD([subQ0])]});var subQ3=sQuery(id+"F2.wireOp",EDGE,"E4.right");var subQ4=sQuery(id+"F2.wireOp",EDGE,"E4.left");var subQ5=sQuery(id+"F2.wireOp",EDGE,"E4.top");var subQ6=sQuery(id+"F2.wireOp",EDGE,"E4.bottom");var subQ7=makeQuery(id+"F3.opExtrude","CAP_FACE",FACE,{"disambiguationData":[OSD([subQ6,subQ5,subQ4,subQ3])],"isStart":false});Q11=makeQuery(id+"F4.opChamfer","BLEND_EDGE",EDGE,{"blendedFrom":[makeQuery(id+"F3.boolean.opBoolean","INTERSECT",EDGE,{"derivedFrom":[subQ2,subQ7]}),makeQuery(id+"F3.boolean.opBoolean","SPLIT",FACE,{"disambiguationData":[TD([makeQuery(id+"F1.opExtrude","SWEPT_FACE",FACE,{"disambiguationData":[OSD([subQ1])]})])],"derivedFrom":makeQuery(id+"F3.opExtrude","SWEPT_FACE",FACE,{"disambiguationData":[OSD([subQ6])]})})],"blendedInto":[makeQuery(id+"F3.boolean.opBoolean","SPLIT",FACE,{"disambiguationData":[TD([makeQuery(id+"F1.opExtrude","SWEPT_FACE",FACE,{"disambiguationData":[OSD([subQ1])]})])],"derivedFrom":makeQuery(id+"F3.opExtrude","SWEPT_FACE",FACE,{"disambiguationData":[OSD([subQ6])]})})]});}
            var Q12;
            {var subQ0=sQuery(id+"F0.wireOp",EDGE,"E0.sketch_text.stroke-57");var subQ1=sQuery(id+"F0.wireOp",EDGE,"E0.sketch_text.stroke-47");var subQ2=makeQuery(id+"F1.opExtrude","SWEPT_FACE",FACE,{"disambiguationData":[OSD([subQ0])]});var subQ3=sQuery(id+"F2.wireOp",EDGE,"E4.right");var subQ4=sQuery(id+"F2.wireOp",EDGE,"E4.left");var subQ5=sQuery(id+"F2.wireOp",EDGE,"E4.top");var subQ6=sQuery(id+"F2.wireOp",EDGE,"E4.bottom");var subQ7=makeQuery(id+"F3.opExtrude","CAP_FACE",FACE,{"disambiguationData":[OSD([subQ6,subQ5,subQ4,subQ3])],"isStart":false});Q12=makeQuery(id+"F4.opChamfer","BLEND_EDGE",EDGE,{"blendedFrom":[makeQuery(id+"F3.boolean.opBoolean","INTERSECT",EDGE,{"derivedFrom":[subQ2,subQ7]}),makeQuery(id+"F3.boolean.opBoolean","SPLIT",FACE,{"disambiguationData":[TD([makeQuery(id+"F1.opExtrude","SWEPT_FACE",FACE,{"disambiguationData":[OSD([subQ1])]})])],"derivedFrom":makeQuery(id+"F3.opExtrude","SWEPT_FACE",FACE,{"disambiguationData":[OSD([subQ6])]})})],"blendedInto":[makeQuery(id+"F3.boolean.opBoolean","SPLIT",FACE,{"disambiguationData":[TD([makeQuery(id+"F1.opExtrude","SWEPT_FACE",FACE,{"disambiguationData":[OSD([subQ1])]})])],"derivedFrom":makeQuery(id+"F3.opExtrude","SWEPT_FACE",FACE,{"disambiguationData":[OSD([subQ6])]})})]});}
            var Q13;
            {var subQ0=sQuery(id+"F2.wireOp",EDGE,"E4.left");Q13=makeQuery(id+"F4.opChamfer","BLEND_EDGE",EDGE,{"blendedFrom":[makeQuery(id+"F3.boolean.opBoolean","INTERSECT",EDGE,{"derivedFrom":[makeQuery(id+"F1.opExtrude","SWEPT_FACE",FACE,{"disambiguationData":[OSD([sQuery(id+"F0.wireOp",EDGE,"E1.sketch_text.stroke-54")])]}),makeQuery(id+"F3.opExtrude","CAP_FACE",FACE,{"disambiguationData":[OSD([sQuery(id+"F2.wireOp",EDGE,"E4.bottom"),sQuery(id+"F2.wireOp",EDGE,"E4.top"),subQ0,sQuery(id+"F2.wireOp",EDGE,"E4.right")])],"isStart":false})]}),makeQuery(id+"F3.opExtrude","SWEPT_FACE",FACE,{"disambiguationData":[OSD([subQ0])]})],"blendedInto":[makeQuery(id+"F3.opExtrude","SWEPT_FACE",FACE,{"disambiguationData":[OSD([subQ0])]})]});}
            var Q14;
            Q14=makeQuery(id+"F3.opExtrude","CAP_EDGE",EDGE,{"disambiguationData":[OSD([sQuery(id+"F2.wireOp",EDGE,"E4.left")])],"isStart":false});
            var Q15;
            {var subQ0=sQuery(id+"F2.wireOp",EDGE,"E4.left");Q15=makeQuery(id+"F4.opChamfer","BLEND_EDGE",EDGE,{"blendedFrom":[makeQuery(id+"F3.boolean.opBoolean","INTERSECT",EDGE,{"derivedFrom":[makeQuery(id+"F1.opExtrude","SWEPT_FACE",FACE,{"disambiguationData":[OSD([sQuery(id+"F0.wireOp",EDGE,"E0.sketch_text.stroke-56")])]}),makeQuery(id+"F3.opExtrude","CAP_FACE",FACE,{"disambiguationData":[OSD([sQuery(id+"F2.wireOp",EDGE,"E4.bottom"),sQuery(id+"F2.wireOp",EDGE,"E4.top"),subQ0,sQuery(id+"F2.wireOp",EDGE,"E4.right")])],"isStart":false})]}),makeQuery(id+"F3.opExtrude","SWEPT_FACE",FACE,{"disambiguationData":[OSD([subQ0])]})],"blendedInto":[makeQuery(id+"F3.opExtrude","SWEPT_FACE",FACE,{"disambiguationData":[OSD([subQ0])]})]});}
            var Q16;
            {var subQ0=sQuery(id+"F0.wireOp",EDGE,"E1.sketch_text.stroke-53");var subQ1=sQuery(id+"F0.wireOp",EDGE,"E1.sketch_text.stroke-50");var subQ2=makeQuery(id+"F1.opExtrude","SWEPT_FACE",FACE,{"disambiguationData":[OSD([subQ0])]});var subQ3=sQuery(id+"F2.wireOp",EDGE,"E4.right");var subQ4=sQuery(id+"F2.wireOp",EDGE,"E4.left");var subQ5=sQuery(id+"F2.wireOp",EDGE,"E4.top");var subQ6=sQuery(id+"F2.wireOp",EDGE,"E4.bottom");var subQ7=makeQuery(id+"F3.opExtrude","CAP_FACE",FACE,{"disambiguationData":[OSD([subQ6,subQ5,subQ4,subQ3])],"isStart":false});Q16=makeQuery(id+"F4.opChamfer","BLEND_EDGE",EDGE,{"blendedFrom":[makeQuery(id+"F3.boolean.opBoolean","INTERSECT",EDGE,{"derivedFrom":[subQ2,subQ7]}),makeQuery(id+"F3.boolean.opBoolean","SPLIT",FACE,{"disambiguationData":[TD([makeQuery(id+"F1.opExtrude","SWEPT_FACE",FACE,{"disambiguationData":[OSD([subQ1])]})])],"derivedFrom":makeQuery(id+"F3.opExtrude","SWEPT_FACE",FACE,{"disambiguationData":[OSD([subQ5])]})})],"blendedInto":[makeQuery(id+"F3.boolean.opBoolean","SPLIT",FACE,{"disambiguationData":[TD([makeQuery(id+"F1.opExtrude","SWEPT_FACE",FACE,{"disambiguationData":[OSD([subQ1])]})])],"derivedFrom":makeQuery(id+"F3.opExtrude","SWEPT_FACE",FACE,{"disambiguationData":[OSD([subQ5])]})})]});}
            var Q17;
            {var subQ0=sQuery(id+"F2.wireOp",EDGE,"E4.top");Q17=makeQuery(id+"F3.boolean.opBoolean","SPLIT",EDGE,{"disambiguationData":[TD([makeQuery(id+"F1.opExtrude","SWEPT_FACE",FACE,{"disambiguationData":[OSD([sQuery(id+"F0.wireOp",EDGE,"E1.sketch_text.stroke-50")])]})])],"derivedFrom":makeQuery(id+"F3.opExtrude","CAP_EDGE",EDGE,{"disambiguationData":[OSD([subQ0])],"isStart":false})});}
            var Q18;
            {var subQ1=sQuery(id+"F0.wireOp",EDGE,"E1.sketch_text.stroke-50");var subQ2=makeQuery(id+"F1.opExtrude","SWEPT_FACE",FACE,{"disambiguationData":[OSD([subQ1])]});var subQ3=sQuery(id+"F2.wireOp",EDGE,"E4.right");var subQ4=sQuery(id+"F2.wireOp",EDGE,"E4.left");var subQ5=sQuery(id+"F2.wireOp",EDGE,"E4.top");var subQ6=sQuery(id+"F2.wireOp",EDGE,"E4.bottom");var subQ7=makeQuery(id+"F3.opExtrude","CAP_FACE",FACE,{"disambiguationData":[OSD([subQ6,subQ5,subQ4,subQ3])],"isStart":false});Q18=makeQuery(id+"F4.opChamfer","BLEND_EDGE",EDGE,{"blendedFrom":[makeQuery(id+"F3.boolean.opBoolean","INTERSECT",EDGE,{"derivedFrom":[subQ2,subQ7]}),makeQuery(id+"F3.boolean.opBoolean","SPLIT",FACE,{"disambiguationData":[TD([subQ2])],"derivedFrom":makeQuery(id+"F3.opExtrude","SWEPT_FACE",FACE,{"disambiguationData":[OSD([subQ5])]})})],"blendedInto":[makeQuery(id+"F3.boolean.opBoolean","SPLIT",FACE,{"disambiguationData":[TD([subQ2])],"derivedFrom":makeQuery(id+"F3.opExtrude","SWEPT_FACE",FACE,{"disambiguationData":[OSD([subQ5])]})})]});}
            var Q19;
            {var subQ0=sQuery(id+"F0.wireOp",EDGE,"E1.sketch_text.stroke-48");var subQ1=sQuery(id+"F0.wireOp",EDGE,"E1.sketch_text.stroke-33");var subQ2=makeQuery(id+"F1.opExtrude","SWEPT_FACE",FACE,{"disambiguationData":[OSD([subQ0])]});var subQ3=sQuery(id+"F2.wireOp",EDGE,"E4.right");var subQ4=sQuery(id+"F2.wireOp",EDGE,"E4.left");var subQ5=sQuery(id+"F2.wireOp",EDGE,"E4.top");var subQ6=sQuery(id+"F2.wireOp",EDGE,"E4.bottom");var subQ7=makeQuery(id+"F3.opExtrude","CAP_FACE",FACE,{"disambiguationData":[OSD([subQ6,subQ5,subQ4,subQ3])],"isStart":false});Q19=makeQuery(id+"F4.opChamfer","BLEND_EDGE",EDGE,{"blendedFrom":[makeQuery(id+"F3.boolean.opBoolean","INTERSECT",EDGE,{"derivedFrom":[subQ2,subQ7]}),makeQuery(id+"F3.boolean.opBoolean","SPLIT",FACE,{"disambiguationData":[TD([makeQuery(id+"F1.opExtrude","SWEPT_FACE",FACE,{"disambiguationData":[OSD([subQ1])]})])],"derivedFrom":makeQuery(id+"F3.opExtrude","SWEPT_FACE",FACE,{"disambiguationData":[OSD([subQ5])]})})],"blendedInto":[makeQuery(id+"F3.boolean.opBoolean","SPLIT",FACE,{"disambiguationData":[TD([makeQuery(id+"F1.opExtrude","SWEPT_FACE",FACE,{"disambiguationData":[OSD([subQ1])]})])],"derivedFrom":makeQuery(id+"F3.opExtrude","SWEPT_FACE",FACE,{"disambiguationData":[OSD([subQ5])]})})]});}
            var Q20;
            {var subQ0=sQuery(id+"F2.wireOp",EDGE,"E4.top");Q20=makeQuery(id+"F3.boolean.opBoolean","SPLIT",EDGE,{"disambiguationData":[TD([makeQuery(id+"F1.opExtrude","SWEPT_FACE",FACE,{"disambiguationData":[OSD([sQuery(id+"F0.wireOp",EDGE,"E1.sketch_text.stroke-33")])]})])],"derivedFrom":makeQuery(id+"F3.opExtrude","CAP_EDGE",EDGE,{"disambiguationData":[OSD([subQ0])],"isStart":false})});}
            var Q21;
            {var subQ1=sQuery(id+"F0.wireOp",EDGE,"E1.sketch_text.stroke-33");var subQ2=makeQuery(id+"F1.opExtrude","SWEPT_FACE",FACE,{"disambiguationData":[OSD([subQ1])]});var subQ3=sQuery(id+"F2.wireOp",EDGE,"E4.right");var subQ4=sQuery(id+"F2.wireOp",EDGE,"E4.left");var subQ5=sQuery(id+"F2.wireOp",EDGE,"E4.top");var subQ6=sQuery(id+"F2.wireOp",EDGE,"E4.bottom");var subQ7=makeQuery(id+"F3.opExtrude","CAP_FACE",FACE,{"disambiguationData":[OSD([subQ6,subQ5,subQ4,subQ3])],"isStart":false});Q21=makeQuery(id+"F4.opChamfer","BLEND_EDGE",EDGE,{"blendedFrom":[makeQuery(id+"F3.boolean.opBoolean","INTERSECT",EDGE,{"derivedFrom":[subQ2,subQ7]}),makeQuery(id+"F3.boolean.opBoolean","SPLIT",FACE,{"disambiguationData":[TD([subQ2])],"derivedFrom":makeQuery(id+"F3.opExtrude","SWEPT_FACE",FACE,{"disambiguationData":[OSD([subQ5])]})})],"blendedInto":[makeQuery(id+"F3.boolean.opBoolean","SPLIT",FACE,{"disambiguationData":[TD([subQ2])],"derivedFrom":makeQuery(id+"F3.opExtrude","SWEPT_FACE",FACE,{"disambiguationData":[OSD([subQ5])]})})]});}
            var Q22;
            {var subQ0=sQuery(id+"F0.wireOp",EDGE,"E1.sketch_text.stroke-31");var subQ1=makeQuery(id+"F1.opExtrude","SWEPT_FACE",FACE,{"disambiguationData":[OSD([subQ0])]});var subQ2=sQuery(id+"F0.wireOp",EDGE,"E1.sketch_text.stroke-29");var subQ3=sQuery(id+"F2.wireOp",EDGE,"E4.right");var subQ4=sQuery(id+"F2.wireOp",EDGE,"E4.left");var subQ5=sQuery(id+"F2.wireOp",EDGE,"E4.top");var subQ6=sQuery(id+"F2.wireOp",EDGE,"E4.bottom");var subQ7=makeQuery(id+"F3.opExtrude","CAP_FACE",FACE,{"disambiguationData":[OSD([subQ6,subQ5,subQ4,subQ3])],"isStart":false});Q22=makeQuery(id+"F4.opChamfer","BLEND_EDGE",EDGE,{"blendedFrom":[makeQuery(id+"F3.boolean.opBoolean","INTERSECT",EDGE,{"derivedFrom":[subQ1,subQ7]}),makeQuery(id+"F3.boolean.opBoolean","SPLIT",FACE,{"disambiguationData":[TD([makeQuery(id+"F1.opExtrude","SWEPT_FACE",FACE,{"disambiguationData":[OSD([subQ2])]})])],"derivedFrom":makeQuery(id+"F3.opExtrude","SWEPT_FACE",FACE,{"disambiguationData":[OSD([subQ5])]})})],"blendedInto":[makeQuery(id+"F3.boolean.opBoolean","SPLIT",FACE,{"disambiguationData":[TD([makeQuery(id+"F1.opExtrude","SWEPT_FACE",FACE,{"disambiguationData":[OSD([subQ2])]})])],"derivedFrom":makeQuery(id+"F3.opExtrude","SWEPT_FACE",FACE,{"disambiguationData":[OSD([subQ5])]})})]});}
            var Q23;
            {var subQ0=sQuery(id+"F2.wireOp",EDGE,"E4.top");Q23=makeQuery(id+"F3.boolean.opBoolean","SPLIT",EDGE,{"disambiguationData":[TD([makeQuery(id+"F1.opExtrude","SWEPT_FACE",FACE,{"disambiguationData":[OSD([sQuery(id+"F0.wireOp",EDGE,"E1.sketch_text.stroke-29")])]})])],"derivedFrom":makeQuery(id+"F3.opExtrude","CAP_EDGE",EDGE,{"disambiguationData":[OSD([subQ0])],"isStart":false})});}
            var Q24;
            {var subQ1=sQuery(id+"F0.wireOp",EDGE,"E1.sketch_text.stroke-29");var subQ2=makeQuery(id+"F1.opExtrude","SWEPT_FACE",FACE,{"disambiguationData":[OSD([subQ1])]});var subQ3=sQuery(id+"F2.wireOp",EDGE,"E4.right");var subQ4=sQuery(id+"F2.wireOp",EDGE,"E4.left");var subQ5=sQuery(id+"F2.wireOp",EDGE,"E4.top");var subQ6=sQuery(id+"F2.wireOp",EDGE,"E4.bottom");var subQ7=makeQuery(id+"F3.opExtrude","CAP_FACE",FACE,{"disambiguationData":[OSD([subQ6,subQ5,subQ4,subQ3])],"isStart":false});Q24=makeQuery(id+"F4.opChamfer","BLEND_EDGE",EDGE,{"blendedFrom":[makeQuery(id+"F3.boolean.opBoolean","INTERSECT",EDGE,{"derivedFrom":[subQ2,subQ7]}),makeQuery(id+"F3.boolean.opBoolean","SPLIT",FACE,{"disambiguationData":[TD([subQ2])],"derivedFrom":makeQuery(id+"F3.opExtrude","SWEPT_FACE",FACE,{"disambiguationData":[OSD([subQ5])]})})],"blendedInto":[makeQuery(id+"F3.boolean.opBoolean","SPLIT",FACE,{"disambiguationData":[TD([subQ2])],"derivedFrom":makeQuery(id+"F3.opExtrude","SWEPT_FACE",FACE,{"disambiguationData":[OSD([subQ5])]})})]});}
            var Q25;
            {var subQ1=sQuery(id+"F0.wireOp",EDGE,"E1.sketch_text.stroke-6");var subQ2=sQuery(id+"F2.wireOp",EDGE,"E4.right");var subQ3=sQuery(id+"F2.wireOp",EDGE,"E4.left");var subQ4=sQuery(id+"F2.wireOp",EDGE,"E4.top");var subQ5=sQuery(id+"F2.wireOp",EDGE,"E4.bottom");var subQ6=makeQuery(id+"F1.opExtrude","SWEPT_FACE",FACE,{"disambiguationData":[OSD([subQ1])]});var subQ7=makeQuery(id+"F3.opExtrude","CAP_FACE",FACE,{"disambiguationData":[OSD([subQ5,subQ4,subQ3,subQ2])],"isStart":false});Q25=makeQuery(id+"F4.opChamfer","BLEND_EDGE",EDGE,{"blendedFrom":[makeQuery(id+"F3.boolean.opBoolean","INTERSECT",EDGE,{"derivedFrom":[subQ6,subQ7]}),makeQuery(id+"F3.boolean.opBoolean","SPLIT",FACE,{"disambiguationData":[TD([subQ6])],"derivedFrom":makeQuery(id+"F3.opExtrude","SWEPT_FACE",FACE,{"disambiguationData":[OSD([subQ4])]})})],"blendedInto":[makeQuery(id+"F3.boolean.opBoolean","SPLIT",FACE,{"disambiguationData":[TD([subQ6])],"derivedFrom":makeQuery(id+"F3.opExtrude","SWEPT_FACE",FACE,{"disambiguationData":[OSD([subQ4])]})})]});}
            var Q26;
            {var subQ0=sQuery(id+"F0.wireOp",EDGE,"E1.sketch_text.stroke-26");var subQ1=sQuery(id+"F0.wireOp",EDGE,"E1.sketch_text.stroke-6");var subQ2=makeQuery(id+"F1.opExtrude","SWEPT_FACE",FACE,{"disambiguationData":[OSD([subQ0])]});var subQ3=sQuery(id+"F2.wireOp",EDGE,"E4.right");var subQ4=sQuery(id+"F2.wireOp",EDGE,"E4.left");var subQ5=sQuery(id+"F2.wireOp",EDGE,"E4.top");var subQ6=sQuery(id+"F2.wireOp",EDGE,"E4.bottom");var subQ7=makeQuery(id+"F3.opExtrude","CAP_FACE",FACE,{"disambiguationData":[OSD([subQ6,subQ5,subQ4,subQ3])],"isStart":false});Q26=makeQuery(id+"F4.opChamfer","BLEND_EDGE",EDGE,{"blendedFrom":[makeQuery(id+"F3.boolean.opBoolean","INTERSECT",EDGE,{"derivedFrom":[subQ2,subQ7]}),makeQuery(id+"F3.boolean.opBoolean","SPLIT",FACE,{"disambiguationData":[TD([makeQuery(id+"F1.opExtrude","SWEPT_FACE",FACE,{"disambiguationData":[OSD([subQ1])]})])],"derivedFrom":makeQuery(id+"F3.opExtrude","SWEPT_FACE",FACE,{"disambiguationData":[OSD([subQ5])]})})],"blendedInto":[makeQuery(id+"F3.boolean.opBoolean","SPLIT",FACE,{"disambiguationData":[TD([makeQuery(id+"F1.opExtrude","SWEPT_FACE",FACE,{"disambiguationData":[OSD([subQ1])]})])],"derivedFrom":makeQuery(id+"F3.opExtrude","SWEPT_FACE",FACE,{"disambiguationData":[OSD([subQ5])]})})]});}
            var Q27;
            {var subQ0=sQuery(id+"F2.wireOp",EDGE,"E4.top");Q27=makeQuery(id+"F3.boolean.opBoolean","SPLIT",EDGE,{"disambiguationData":[TD([makeQuery(id+"F1.opExtrude","SWEPT_FACE",FACE,{"disambiguationData":[OSD([sQuery(id+"F0.wireOp",EDGE,"E1.sketch_text.stroke-6")])]})])],"derivedFrom":makeQuery(id+"F3.opExtrude","CAP_EDGE",EDGE,{"disambiguationData":[OSD([subQ0])],"isStart":false})});}
            var Q28;
            {var subQ0=sQuery(id+"F2.wireOp",EDGE,"E4.right");Q28=makeQuery(id+"F4.opChamfer","BLEND_EDGE",EDGE,{"blendedFrom":[makeQuery(id+"F3.boolean.opBoolean","INTERSECT",EDGE,{"derivedFrom":[makeQuery(id+"F1.opExtrude","SWEPT_FACE",FACE,{"disambiguationData":[OSD([sQuery(id+"F0.wireOp",EDGE,"E0.sketch_text.stroke-2")])]}),makeQuery(id+"F3.opExtrude","CAP_FACE",FACE,{"disambiguationData":[OSD([sQuery(id+"F2.wireOp",EDGE,"E4.bottom"),sQuery(id+"F2.wireOp",EDGE,"E4.top"),sQuery(id+"F2.wireOp",EDGE,"E4.left"),subQ0])],"isStart":false})]}),makeQuery(id+"F3.opExtrude","SWEPT_FACE",FACE,{"disambiguationData":[OSD([subQ0])]})],"blendedInto":[makeQuery(id+"F3.opExtrude","SWEPT_FACE",FACE,{"disambiguationData":[OSD([subQ0])]})]});}
            var Q29;
            Q29=makeQuery(id+"F3.opExtrude","CAP_EDGE",EDGE,{"disambiguationData":[OSD([sQuery(id+"F2.wireOp",EDGE,"E4.right")])],"isStart":false});
            var Q30;
            {var subQ0=sQuery(id+"F2.wireOp",EDGE,"E4.right");Q30=makeQuery(id+"F4.opChamfer","BLEND_EDGE",EDGE,{"blendedFrom":[makeQuery(id+"F3.boolean.opBoolean","INTERSECT",EDGE,{"derivedFrom":[makeQuery(id+"F1.opExtrude","SWEPT_FACE",FACE,{"disambiguationData":[OSD([sQuery(id+"F0.wireOp",EDGE,"E1.sketch_text.stroke-5")])]}),makeQuery(id+"F3.opExtrude","CAP_FACE",FACE,{"disambiguationData":[OSD([sQuery(id+"F2.wireOp",EDGE,"E4.bottom"),sQuery(id+"F2.wireOp",EDGE,"E4.top"),sQuery(id+"F2.wireOp",EDGE,"E4.left"),subQ0])],"isStart":false})]}),makeQuery(id+"F3.opExtrude","SWEPT_FACE",FACE,{"disambiguationData":[OSD([subQ0])]})],"blendedInto":[makeQuery(id+"F3.opExtrude","SWEPT_FACE",FACE,{"disambiguationData":[OSD([subQ0])]})]});}
            fillet(context, id + "F7", {"entities" : qUnion([Q0, Q1, Q2, Q3, Q4, Q5, Q6, Q7, Q8, Q9, Q10, Q11, Q12, Q13, Q14, Q15, Q16, Q17, Q18, Q19, Q20, Q21, Q22, Q23, Q24, Q25, Q26, Q27, Q28, Q29, Q30]), "radius" : 1.5 * mm, "tangentPropagation" : true, "allowEdgeOverflow" : false});
        }
    });
